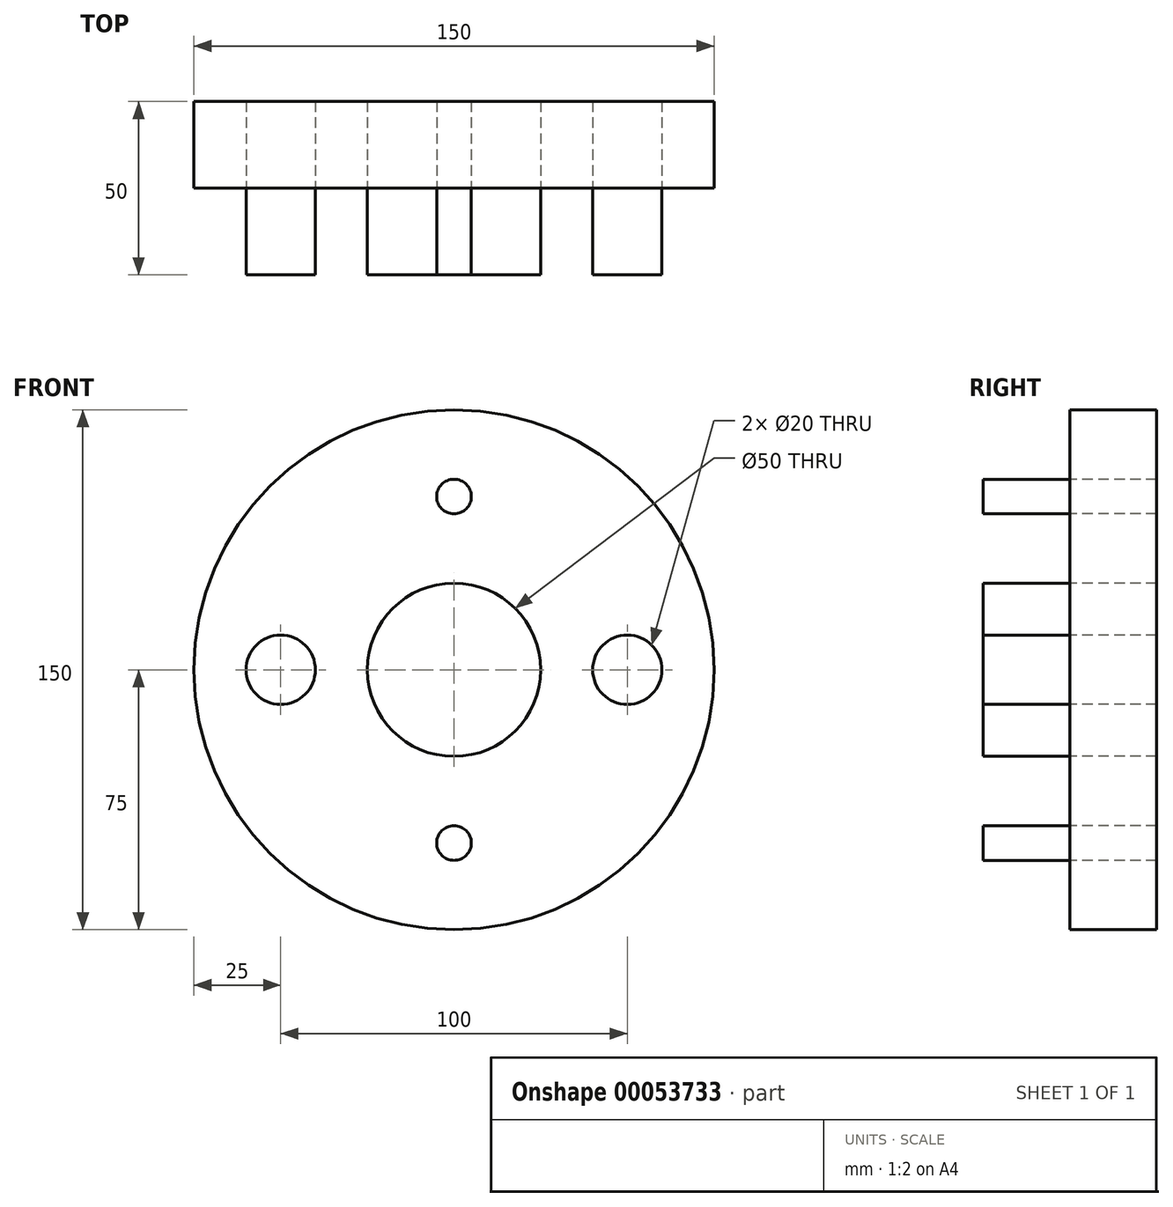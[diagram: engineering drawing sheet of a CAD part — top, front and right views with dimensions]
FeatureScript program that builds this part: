
annotation { "Feature Type Name" : "Feature", "Feature Type Description" : "" }
export const myFeature = defineFeature(function(context is Context, id is Id, definition is map)
    precondition{}
    {
        {
            var Q0;
            Q0=qCreatedBy(makeId("Front.planeOp"),FACE);
            var sketch = newSketch(context, id + "F0", { "sketchPlane" : qUnion([Q0])});
            skCircle(sketch, "E0", {"center": v(0, 0) * mm, "radius": 75 * mm});
            skCircle(sketch, "E1", {"center": v(0, 50) * mm, "radius": 5 * mm});
            skCircle(sketch, "E2", {"center": v(0, -50) * mm, "radius": 5 * mm});
            skCircle(sketch, "E3", {"center": v(50, 0) * mm, "radius": 10 * mm});
            skCircle(sketch, "E4", {"center": v(-50, 0) * mm, "radius": 10 * mm});
            skCircle(sketch, "E5", {"center": v(0, 0) * mm, "radius": 25 * mm});
            skSolve(sketch);
        }
        {
            var Q0;
            Q0=makeQuery(id+"F0.imprint","IMPRINT",FACE,{"disambiguationData":[TD([[makeQuery(id+"F0.imprint","IMPRINT",EDGE,{"derivedFrom":sQuery(id+"F0.wireOp",EDGE,"E4")}),1.0]])]});
            var Q1;
            Q1=makeQuery(id+"F0.imprint","IMPRINT",FACE,{"disambiguationData":[TD([[makeQuery(id+"F0.imprint","IMPRINT",EDGE,{"derivedFrom":sQuery(id+"F0.wireOp",EDGE,"E1")}),1.0]])]});
            var Q2;
            Q2=makeQuery(id+"F0.imprint","IMPRINT",FACE,{"disambiguationData":[TD([[makeQuery(id+"F0.imprint","IMPRINT",EDGE,{"derivedFrom":sQuery(id+"F0.wireOp",EDGE,"E3")}),1.0]])]});
            var Q3;
            Q3=makeQuery(id+"F0.imprint","IMPRINT",FACE,{"disambiguationData":[TD([[makeQuery(id+"F0.imprint","IMPRINT",EDGE,{"derivedFrom":sQuery(id+"F0.wireOp",EDGE,"E2")}),1.0]])]});
            var Q4;
            Q4=makeQuery(id+"F0.imprint","IMPRINT",FACE,{"disambiguationData":[TD([[makeQuery(id+"F0.imprint","IMPRINT",EDGE,{"derivedFrom":sQuery(id+"F0.wireOp",EDGE,"E5")}),1.0]])]});
            extrude(context, id + "F1", {"entities" : qUnion([Q0, Q1, Q2, Q3, Q4]), "depth" : 25 * mm});
        }
        {
            var Q0;
            Q0=makeQuery(id+"F0.imprint","IMPRINT",FACE,{"disambiguationData":[TD([[makeQuery(id+"F0.imprint","IMPRINT",EDGE,{"derivedFrom":sQuery(id+"F0.wireOp",EDGE,"E0")}),1.0]])]});
            extrude(context, id + "F2", {"entities" : qUnion([Q0]), "oppositeDirection" : true, "depth" : 25 * mm});
        }
    });
